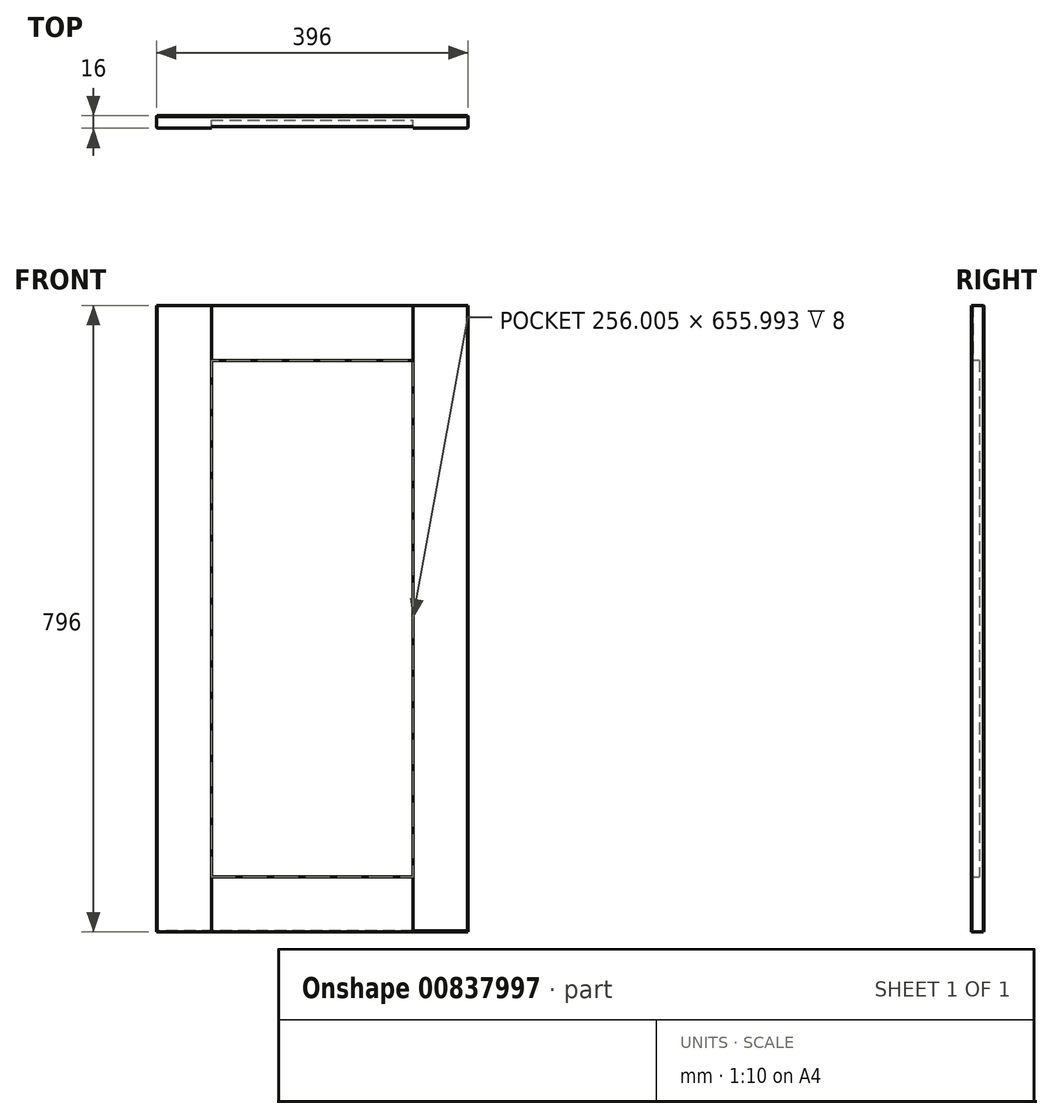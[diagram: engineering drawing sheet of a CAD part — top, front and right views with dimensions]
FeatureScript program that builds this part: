
annotation { "Feature Type Name" : "Feature", "Feature Type Description" : "" }
export const myFeature = defineFeature(function(context is Context, id is Id, definition is map)
    precondition{}
    {
        {
            var Q0;
            Q0=qCreatedBy(makeId("Front.planeOp"),FACE);
            var sketch = newSketch(context, id + "F0", { "sketchPlane" : qUnion([Q0])});
            skLineSegment(sketch, "E0.bottom", {"start": v(0, 0) * mm, "end": v(35.9, 0) * mm});
            skLineSegment(sketch, "E0.top", {"start": v(0, 30.12) * mm, "end": v(35.9, 30.12) * mm});
            skLineSegment(sketch, "E0.left", {"start": v(0, 0) * mm, "end": v(0, 30.12) * mm});
            skLineSegment(sketch, "E0.right", {"start": v(35.9, 0) * mm, "end": v(35.9, 30.12) * mm});
            skSolve(sketch);
        }
        {
            var Q0;
            Q0=makeQuery(id+"F0.imprint","IMPRINT",FACE,{"disambiguationData":[TD([[makeQuery(id+"F0.imprint","IMPRINT",EDGE,{"derivedFrom":sQuery(id+"F0.wireOp",EDGE,"E0.bottom")}),1.0]])]});
            extrude(context, id + "F1", {"entities" : qUnion([Q0]), "depth" : 16 * mm, "offsetDistance" : 25.4 * mm});
        }
        {
            var Q0;
            Q0=makeQuery(id+"F1.opExtrude","SWEPT_FACE",FACE,{"disambiguationData":[OSD([sQuery(id+"F0.wireOp",EDGE,"E0.left")])]});
            extrude(context, id + "F2", {"entities" : qUnion([Q0]), "operationType" : NewBodyOperationType.ADD, "oppositeDirection" : true, "depth" : 196 * mm, "offsetDistance" : 25 * mm});
        }
        {
            var Q0;
            {var subQ0=sQuery(id+"F0.wireOp",EDGE,"E0.bottom");Q0=makeQuery(id+"F2.boolean.opBoolean","MERGE",FACE,{"derivedFrom":[makeQuery(id+"F1.opExtrude","SWEPT_FACE",FACE,{"disambiguationData":[OSD([subQ0])]}),makeQuery(id+"F2.opExtrude","SWEPT_FACE",FACE,{"disambiguationData":[OSD([subQ0,sQuery(id+"F0.wireOp",EDGE,"E0.left")])]})]});}
            extrude(context, id + "F3", {"entities" : qUnion([Q0]), "operationType" : NewBodyOperationType.ADD, "oppositeDirection" : true, "depth" : 796 * mm, "offsetDistance" : 25 * mm});
        }
        {
            var Q0;
            {var subQ0=sQuery(id+"F0.wireOp",EDGE,"E0.left");var subQ1=sQuery(id+"F0.wireOp",EDGE,"E0.bottom");Q0=makeQuery(id+"F3.boolean.opBoolean","MERGE",FACE,{"derivedFrom":[makeQuery(id+"F2.boolean.opBoolean","MERGE",FACE,{"derivedFrom":[makeQuery(id+"F1.opExtrude","CAP_FACE",FACE,{"disambiguationData":[OSD([subQ1,sQuery(id+"F0.wireOp",EDGE,"E0.top"),subQ0,sQuery(id+"F0.wireOp",EDGE,"E0.right")])],"isStart":false}),makeQuery(id+"F2.opExtrude","SWEPT_FACE",FACE,{"disambiguationData":[OSD([subQ0]),TDD([makeQuery(id+"F1.opExtrude","CAP_EDGE",EDGE,{"disambiguationData":[OSD([subQ0])],"isStart":false})])]})]}),makeQuery(id+"F3.opExtrude","SWEPT_FACE",FACE,{"disambiguationData":[OSD([subQ1,subQ0]),TDD([makeQuery(id+"F2.boolean.opBoolean","MERGE",EDGE,{"derivedFrom":[makeQuery(id+"F1.opExtrude","CAP_EDGE",EDGE,{"disambiguationData":[OSD([subQ1])],"isStart":false}),makeQuery(id+"F2.opExtrude","SWEPT_EDGE",EDGE,{"disambiguationData":[OSD([subQ1,subQ0]),TDD([makeQuery(id+"F1.opExtrude","CAP_VERTEX",VERTEX,{"disambiguationData":[OSD([subQ1,subQ0])],"isStart":false})])]})]})])]})]});}
            var sketch = newSketch(context, id + "F4", { "sketchPlane" : qUnion([Q0])});
            skLineSegment(sketch, "E1.bottom", {"start": v(0, 796) * mm, "end": v(42.19, 796) * mm});
            skLineSegment(sketch, "E1.top", {"start": v(0, 751.57) * mm, "end": v(42.19, 751.57) * mm});
            skLineSegment(sketch, "E1.left", {"start": v(0, 796) * mm, "end": v(0, 751.57) * mm});
            skLineSegment(sketch, "E1.right", {"start": v(42.19, 796) * mm, "end": v(42.19, 751.57) * mm});
            skLineSegment(sketch, "E2.bottom", {"start": v(196, 796) * mm, "end": v(153.6, 796) * mm});
            skLineSegment(sketch, "E2.top", {"start": v(196, 746.75) * mm, "end": v(153.6, 746.75) * mm});
            skLineSegment(sketch, "E2.left", {"start": v(196, 796) * mm, "end": v(196, 746.75) * mm});
            skLineSegment(sketch, "E2.right", {"start": v(153.6, 796) * mm, "end": v(153.6, 746.75) * mm});
            skSolve(sketch);
        }
        {
            var Q0;
            Q0=makeQuery(id+"F4.imprint","IMPRINT",FACE,{"disambiguationData":[TD([[makeQuery(id+"F4.imprint","IMPRINT",EDGE,{"derivedFrom":sQuery(id+"F4.wireOp",EDGE,"E1.bottom")}),-1.0]])]});
            var Q1;
            Q1=makeQuery(id+"F4.imprint","IMPRINT",FACE,{"disambiguationData":[TD([[makeQuery(id+"F4.imprint","IMPRINT",EDGE,{"derivedFrom":sQuery(id+"F4.wireOp",EDGE,"E2.bottom")}),-1.0]])]});
            extrude(context, id + "F5", {"entities" : qUnion([Q0, Q1]), "operationType" : NewBodyOperationType.ADD, "depth" : 25 * mm, "offsetDistance" : 25 * mm});
        }
        {
            var Q0;
            {var subQ0=sQuery(id+"F0.wireOp",EDGE,"E0.left");var subQ1=sQuery(id+"F0.wireOp",EDGE,"E0.bottom");Q0=makeQuery(id+"F3.boolean.opBoolean","MERGE",FACE,{"derivedFrom":[makeQuery(id+"F2.boolean.opBoolean","MERGE",FACE,{"derivedFrom":[makeQuery(id+"F1.opExtrude","CAP_FACE",FACE,{"disambiguationData":[OSD([subQ1,sQuery(id+"F0.wireOp",EDGE,"E0.top"),subQ0,sQuery(id+"F0.wireOp",EDGE,"E0.right")])],"isStart":false}),makeQuery(id+"F2.opExtrude","SWEPT_FACE",FACE,{"disambiguationData":[OSD([subQ0]),TDD([makeQuery(id+"F1.opExtrude","CAP_EDGE",EDGE,{"disambiguationData":[OSD([subQ0])],"isStart":false})])]})]}),makeQuery(id+"F3.opExtrude","SWEPT_FACE",FACE,{"disambiguationData":[OSD([subQ1,subQ0]),TDD([makeQuery(id+"F2.boolean.opBoolean","MERGE",EDGE,{"derivedFrom":[makeQuery(id+"F1.opExtrude","CAP_EDGE",EDGE,{"disambiguationData":[OSD([subQ1])],"isStart":false}),makeQuery(id+"F2.opExtrude","SWEPT_EDGE",EDGE,{"disambiguationData":[OSD([subQ1,subQ0]),TDD([makeQuery(id+"F1.opExtrude","CAP_VERTEX",VERTEX,{"disambiguationData":[OSD([subQ1,subQ0])],"isStart":false})])]})]})])]})]});}
            var sketch = newSketch(context, id + "F6", { "sketchPlane" : qUnion([Q0])});
            skLineSegment(sketch, "E3.bottom", {"start": v(196, 0) * mm, "end": v(163.38, 0) * mm});
            skLineSegment(sketch, "E3.top", {"start": v(196, 46.55) * mm, "end": v(163.38, 46.55) * mm});
            skLineSegment(sketch, "E3.left", {"start": v(196, 0) * mm, "end": v(196, 46.55) * mm});
            skLineSegment(sketch, "E3.right", {"start": v(163.38, 0) * mm, "end": v(163.38, 46.55) * mm});
            skLineSegment(sketch, "E4.bottom", {"start": v(0, 0) * mm, "end": v(50.28, 0) * mm});
            skLineSegment(sketch, "E4.top", {"start": v(0, 44.4) * mm, "end": v(50.28, 44.4) * mm});
            skLineSegment(sketch, "E4.left", {"start": v(0, 0) * mm, "end": v(0, 44.4) * mm});
            skLineSegment(sketch, "E4.right", {"start": v(50.28, 0) * mm, "end": v(50.28, 44.4) * mm});
            skSolve(sketch);
        }
        {
            var Q0;
            Q0=makeQuery(id+"F6.imprint","IMPRINT",FACE,{"disambiguationData":[TD([[makeQuery(id+"F6.imprint","IMPRINT",EDGE,{"derivedFrom":sQuery(id+"F6.wireOp",EDGE,"E3.bottom")}),1.0]])]});
            var Q1;
            Q1=makeQuery(id+"F6.imprint","IMPRINT",FACE,{"disambiguationData":[TD([[makeQuery(id+"F6.imprint","IMPRINT",EDGE,{"derivedFrom":sQuery(id+"F6.wireOp",EDGE,"E4.bottom")}),1.0]])]});
            extrude(context, id + "F7", {"entities" : qUnion([Q0, Q1]), "operationType" : NewBodyOperationType.ADD, "depth" : 25 * mm, "offsetDistance" : 25 * mm});
        }
        {
            var Q0;
            Q0=makeQuery(id+"F7.opExtrude","SWEPT_FACE",FACE,{"disambiguationData":[OSD([sQuery(id+"F6.wireOp",EDGE,"E4.right")])]});
            extrude(context, id + "F8", {"entities" : qUnion([Q0]), "operationType" : NewBodyOperationType.ADD, "depth" : 19.72 * mm, "offsetDistance" : 25 * mm});
        }
        {
            var Q0;
            {var subQ0=sQuery(id+"F6.wireOp",EDGE,"E4.top");Q0=makeQuery(id+"F8.boolean.opBoolean","MERGE",FACE,{"derivedFrom":[makeQuery(id+"F7.opExtrude","SWEPT_FACE",FACE,{"disambiguationData":[OSD([subQ0])]}),makeQuery(id+"F8.opExtrude","SWEPT_FACE",FACE,{"disambiguationData":[OSD([subQ0,sQuery(id+"F6.wireOp",EDGE,"E4.right")])]})]});}
            extrude(context, id + "F9", {"entities" : qUnion([Q0]), "operationType" : NewBodyOperationType.ADD, "depth" : 25.6 * mm, "offsetDistance" : 25 * mm});
        }
        {
            var Q0;
            Q0=makeQuery(id+"F7.opExtrude","SWEPT_FACE",FACE,{"disambiguationData":[OSD([sQuery(id+"F6.wireOp",EDGE,"E3.right")])]});
            extrude(context, id + "F10", {"entities" : qUnion([Q0]), "operationType" : NewBodyOperationType.ADD, "depth" : 37.38 * mm, "offsetDistance" : 25 * mm});
        }
        {
            var Q0;
            {var subQ0=sQuery(id+"F6.wireOp",EDGE,"E3.top");Q0=makeQuery(id+"F10.boolean.opBoolean","MERGE",FACE,{"derivedFrom":[makeQuery(id+"F7.opExtrude","SWEPT_FACE",FACE,{"disambiguationData":[OSD([subQ0])]}),makeQuery(id+"F10.opExtrude","SWEPT_FACE",FACE,{"disambiguationData":[OSD([subQ0,sQuery(id+"F6.wireOp",EDGE,"E3.right")])]})]});}
            extrude(context, id + "F11", {"entities" : qUnion([Q0]), "operationType" : NewBodyOperationType.ADD, "depth" : 23.45 * mm, "offsetDistance" : 25 * mm});
        }
        {
            var Q0;
            Q0=makeQuery(id+"F5.opExtrude","SWEPT_FACE",FACE,{"disambiguationData":[OSD([sQuery(id+"F4.wireOp",EDGE,"E1.right")])]});
            extrude(context, id + "F12", {"entities" : qUnion([Q0]), "operationType" : NewBodyOperationType.ADD, "depth" : 27.8 * mm, "offsetDistance" : 25 * mm});
        }
        {
            var Q0;
            {var subQ0=sQuery(id+"F4.wireOp",EDGE,"E1.top");Q0=makeQuery(id+"F12.boolean.opBoolean","MERGE",FACE,{"derivedFrom":[makeQuery(id+"F5.opExtrude","SWEPT_FACE",FACE,{"disambiguationData":[OSD([subQ0])]}),makeQuery(id+"F12.opExtrude","SWEPT_FACE",FACE,{"disambiguationData":[OSD([subQ0,sQuery(id+"F4.wireOp",EDGE,"E1.right")])]})]});}
            extrude(context, id + "F13", {"entities" : qUnion([Q0]), "operationType" : NewBodyOperationType.ADD, "depth" : 25.57 * mm, "offsetDistance" : 25 * mm});
        }
        {
            var Q0;
            Q0=makeQuery(id+"F5.opExtrude","SWEPT_FACE",FACE,{"disambiguationData":[OSD([sQuery(id+"F4.wireOp",EDGE,"E2.top")])]});
            extrude(context, id + "F14", {"entities" : qUnion([Q0]), "operationType" : NewBodyOperationType.ADD, "depth" : 20.75 * mm, "offsetDistance" : 25 * mm});
        }
        {
            var Q0;
            {var subQ0=sQuery(id+"F4.wireOp",EDGE,"E2.right");Q0=makeQuery(id+"F14.boolean.opBoolean","MERGE",FACE,{"derivedFrom":[makeQuery(id+"F5.opExtrude","SWEPT_FACE",FACE,{"disambiguationData":[OSD([subQ0])]}),makeQuery(id+"F14.opExtrude","SWEPT_FACE",FACE,{"disambiguationData":[OSD([sQuery(id+"F4.wireOp",EDGE,"E2.top"),subQ0])]})]});}
            extrude(context, id + "F15", {"entities" : qUnion([Q0]), "operationType" : NewBodyOperationType.ADD, "depth" : 27.6 * mm, "offsetDistance" : 25 * mm});
        }
        {
            var Q0;
            {var subQ0=sQuery(id+"F0.wireOp",EDGE,"E0.left");var subQ1=sQuery(id+"F0.wireOp",EDGE,"E0.bottom");Q0=makeQuery(id+"F3.boolean.opBoolean","MERGE",FACE,{"derivedFrom":[makeQuery(id+"F2.boolean.opBoolean","MERGE",FACE,{"derivedFrom":[makeQuery(id+"F1.opExtrude","CAP_FACE",FACE,{"disambiguationData":[OSD([subQ1,sQuery(id+"F0.wireOp",EDGE,"E0.top"),subQ0,sQuery(id+"F0.wireOp",EDGE,"E0.right")])],"isStart":false}),makeQuery(id+"F2.opExtrude","SWEPT_FACE",FACE,{"disambiguationData":[OSD([subQ0]),TDD([makeQuery(id+"F1.opExtrude","CAP_EDGE",EDGE,{"disambiguationData":[OSD([subQ0])],"isStart":false})])]})]}),makeQuery(id+"F3.opExtrude","SWEPT_FACE",FACE,{"disambiguationData":[OSD([subQ1,subQ0]),TDD([makeQuery(id+"F2.boolean.opBoolean","MERGE",EDGE,{"derivedFrom":[makeQuery(id+"F1.opExtrude","CAP_EDGE",EDGE,{"disambiguationData":[OSD([subQ1])],"isStart":false}),makeQuery(id+"F2.opExtrude","SWEPT_EDGE",EDGE,{"disambiguationData":[OSD([subQ1,subQ0]),TDD([makeQuery(id+"F1.opExtrude","CAP_VERTEX",VERTEX,{"disambiguationData":[OSD([subQ1,subQ0])],"isStart":false})])]})]})])]})]});}
            var sketch = newSketch(context, id + "F16", { "sketchPlane" : qUnion([Q0])});
            skLineSegment(sketch, "E5.bottom", {"start": v(70, 726) * mm, "end": v(126, 726) * mm});
            skLineSegment(sketch, "E5.top", {"start": v(70, 70) * mm, "end": v(126, 70) * mm});
            skLineSegment(sketch, "E5.left", {"start": v(70, 726) * mm, "end": v(70, 70) * mm});
            skLineSegment(sketch, "E5.right", {"start": v(126, 726) * mm, "end": v(126, 70) * mm});
            skSolve(sketch);
        }
        {
            var Q0;
            Q0=makeQuery(id+"F16.imprint","IMPRINT",FACE,{"disambiguationData":[TD([[makeQuery(id+"F16.imprint","IMPRINT",EDGE,{"derivedFrom":sQuery(id+"F16.wireOp",EDGE,"E5.top")}),1.0]])]});
            extrude(context, id + "F17", {"entities" : qUnion([Q0]), "operationType" : NewBodyOperationType.REMOVE, "oppositeDirection" : true, "depth" : 10 * mm, "offsetDistance" : 25 * mm});
        }
        {
            var Q0;
            {var subQ2=sQuery(id+"F0.wireOp",EDGE,"E0.left");var subQ3=sQuery(id+"F0.wireOp",EDGE,"E0.bottom");var subQ4=makeQuery(id+"F1.opExtrude","CAP_FACE",FACE,{"disambiguationData":[OSD([subQ3,sQuery(id+"F0.wireOp",EDGE,"E0.top"),subQ2,sQuery(id+"F0.wireOp",EDGE,"E0.right")])],"isStart":false});var subQ7=makeQuery(id+"F3.opExtrude","SWEPT_FACE",FACE,{"disambiguationData":[OSD([subQ3,subQ2]),TDD([makeQuery(id+"F2.boolean.opBoolean","MERGE",EDGE,{"derivedFrom":[makeQuery(id+"F1.opExtrude","CAP_EDGE",EDGE,{"disambiguationData":[OSD([subQ3])],"isStart":false}),makeQuery(id+"F2.opExtrude","SWEPT_EDGE",EDGE,{"disambiguationData":[OSD([subQ3,subQ2]),TDD([makeQuery(id+"F1.opExtrude","CAP_VERTEX",VERTEX,{"disambiguationData":[OSD([subQ3,subQ2])],"isStart":false})])]})]})])]});var subQ8=makeQuery(id+"F2.opExtrude","SWEPT_FACE",FACE,{"disambiguationData":[OSD([subQ2]),TDD([makeQuery(id+"F1.opExtrude","CAP_EDGE",EDGE,{"disambiguationData":[OSD([subQ2])],"isStart":false})])]});Q0=makeQuery(id+"F17.boolean.opBoolean","SPLIT",FACE,{"disambiguationData":[TD([makeQuery(id+"F1.opExtrude","SWEPT_FACE",FACE,{"disambiguationData":[OSD([subQ3])]})])],"derivedFrom":makeQuery(id+"F3.boolean.opBoolean","MERGE",FACE,{"derivedFrom":[makeQuery(id+"F2.boolean.opBoolean","MERGE",FACE,{"derivedFrom":[subQ4,subQ8]}),subQ7]})});}
            var Q1;
            {var subQ2=sQuery(id+"F4.wireOp",EDGE,"E1.bottom");var subQ3=sQuery(id+"F0.wireOp",EDGE,"E0.left");var subQ4=sQuery(id+"F0.wireOp",EDGE,"E0.bottom");var subQ6=makeQuery(id+"F1.opExtrude","CAP_FACE",FACE,{"disambiguationData":[OSD([subQ4,sQuery(id+"F0.wireOp",EDGE,"E0.top"),subQ3,sQuery(id+"F0.wireOp",EDGE,"E0.right")])],"isStart":false});var subQ7=makeQuery(id+"F2.opExtrude","SWEPT_FACE",FACE,{"disambiguationData":[OSD([subQ3]),TDD([makeQuery(id+"F1.opExtrude","CAP_EDGE",EDGE,{"disambiguationData":[OSD([subQ3])],"isStart":false})])]});var subQ8=makeQuery(id+"F3.opExtrude","SWEPT_FACE",FACE,{"disambiguationData":[OSD([subQ4,subQ3]),TDD([makeQuery(id+"F2.boolean.opBoolean","MERGE",EDGE,{"derivedFrom":[makeQuery(id+"F1.opExtrude","CAP_EDGE",EDGE,{"disambiguationData":[OSD([subQ4])],"isStart":false}),makeQuery(id+"F2.opExtrude","SWEPT_EDGE",EDGE,{"disambiguationData":[OSD([subQ4,subQ3]),TDD([makeQuery(id+"F1.opExtrude","CAP_VERTEX",VERTEX,{"disambiguationData":[OSD([subQ4,subQ3])],"isStart":false})])]})]})])]});Q1=makeQuery(id+"F17.boolean.opBoolean","SPLIT",FACE,{"disambiguationData":[TD([makeQuery(id+"F5.opExtrude","SWEPT_FACE",FACE,{"disambiguationData":[OSD([subQ2])]})])],"derivedFrom":makeQuery(id+"F3.boolean.opBoolean","MERGE",FACE,{"derivedFrom":[makeQuery(id+"F2.boolean.opBoolean","MERGE",FACE,{"derivedFrom":[subQ6,subQ7]}),subQ8]})});}
            extrude(context, id + "F18", {"entities" : qUnion([Q0, Q1]), "operationType" : NewBodyOperationType.REMOVE, "oppositeDirection" : true, "depth" : 2 * mm, "offsetDistance" : 25 * mm});
        }
        {
            var Q0;
            {var subQ0=sQuery(id+"F4.wireOp",EDGE,"E1.right");var subQ1=sQuery(id+"F4.wireOp",EDGE,"E1.top");Q0=makeQuery(id+"F13.boolean.opBoolean","MERGE",FACE,{"derivedFrom":[makeQuery(id+"F12.boolean.opBoolean","MERGE",FACE,{"derivedFrom":[makeQuery(id+"F5.opExtrude","CAP_FACE",FACE,{"disambiguationData":[OSD([sQuery(id+"F4.wireOp",EDGE,"E1.bottom"),subQ1,sQuery(id+"F4.wireOp",EDGE,"E1.left"),subQ0])],"isStart":false}),makeQuery(id+"F12.opExtrude","SWEPT_FACE",FACE,{"disambiguationData":[OSD([subQ0]),TDD([makeQuery(id+"F5.opExtrude","CAP_EDGE",EDGE,{"disambiguationData":[OSD([subQ0])],"isStart":false})])]})]}),makeQuery(id+"F13.opExtrude","SWEPT_FACE",FACE,{"disambiguationData":[OSD([subQ1,subQ0]),TDD([makeQuery(id+"F12.boolean.opBoolean","MERGE",EDGE,{"derivedFrom":[makeQuery(id+"F5.opExtrude","CAP_EDGE",EDGE,{"disambiguationData":[OSD([subQ1])],"isStart":false}),makeQuery(id+"F12.opExtrude","SWEPT_EDGE",EDGE,{"disambiguationData":[OSD([subQ1,subQ0]),TDD([makeQuery(id+"F5.opExtrude","CAP_VERTEX",VERTEX,{"disambiguationData":[OSD([subQ1,subQ0])],"isStart":false})])]})]})])]})]});}
            var Q1;
            {var subQ0=sQuery(id+"F4.wireOp",EDGE,"E2.right");var subQ1=sQuery(id+"F4.wireOp",EDGE,"E2.top");Q1=makeQuery(id+"F15.boolean.opBoolean","MERGE",FACE,{"derivedFrom":[makeQuery(id+"F14.boolean.opBoolean","MERGE",FACE,{"derivedFrom":[makeQuery(id+"F5.opExtrude","CAP_FACE",FACE,{"disambiguationData":[OSD([sQuery(id+"F4.wireOp",EDGE,"E2.bottom"),subQ1,sQuery(id+"F4.wireOp",EDGE,"E2.left"),subQ0])],"isStart":false}),makeQuery(id+"F14.opExtrude","SWEPT_FACE",FACE,{"disambiguationData":[OSD([subQ1]),TDD([makeQuery(id+"F5.opExtrude","CAP_EDGE",EDGE,{"disambiguationData":[OSD([subQ1])],"isStart":false})])]})]}),makeQuery(id+"F15.opExtrude","SWEPT_FACE",FACE,{"disambiguationData":[OSD([subQ1,subQ0]),TDD([makeQuery(id+"F14.boolean.opBoolean","MERGE",EDGE,{"derivedFrom":[makeQuery(id+"F5.opExtrude","CAP_EDGE",EDGE,{"disambiguationData":[OSD([subQ0])],"isStart":false}),makeQuery(id+"F14.opExtrude","SWEPT_EDGE",EDGE,{"disambiguationData":[OSD([subQ1,subQ0]),TDD([makeQuery(id+"F5.opExtrude","CAP_VERTEX",VERTEX,{"disambiguationData":[OSD([subQ1,subQ0])],"isStart":false})])]})]})])]})]});}
            var Q2;
            {var subQ0=sQuery(id+"F6.wireOp",EDGE,"E4.right");var subQ1=sQuery(id+"F6.wireOp",EDGE,"E4.top");Q2=makeQuery(id+"F9.boolean.opBoolean","MERGE",FACE,{"derivedFrom":[makeQuery(id+"F8.boolean.opBoolean","MERGE",FACE,{"derivedFrom":[makeQuery(id+"F7.opExtrude","CAP_FACE",FACE,{"disambiguationData":[OSD([sQuery(id+"F6.wireOp",EDGE,"E4.bottom"),subQ1,sQuery(id+"F6.wireOp",EDGE,"E4.left"),subQ0])],"isStart":false}),makeQuery(id+"F8.opExtrude","SWEPT_FACE",FACE,{"disambiguationData":[OSD([subQ0]),TDD([makeQuery(id+"F7.opExtrude","CAP_EDGE",EDGE,{"disambiguationData":[OSD([subQ0])],"isStart":false})])]})]}),makeQuery(id+"F9.opExtrude","SWEPT_FACE",FACE,{"disambiguationData":[OSD([subQ1,subQ0]),TDD([makeQuery(id+"F8.boolean.opBoolean","MERGE",EDGE,{"derivedFrom":[makeQuery(id+"F7.opExtrude","CAP_EDGE",EDGE,{"disambiguationData":[OSD([subQ1])],"isStart":false}),makeQuery(id+"F8.opExtrude","SWEPT_EDGE",EDGE,{"disambiguationData":[OSD([subQ1,subQ0]),TDD([makeQuery(id+"F7.opExtrude","CAP_VERTEX",VERTEX,{"disambiguationData":[OSD([subQ1,subQ0])],"isStart":false})])]})]})])]})]});}
            var Q3;
            {var subQ0=sQuery(id+"F6.wireOp",EDGE,"E3.right");var subQ1=sQuery(id+"F6.wireOp",EDGE,"E3.top");Q3=makeQuery(id+"F11.boolean.opBoolean","MERGE",FACE,{"derivedFrom":[makeQuery(id+"F10.boolean.opBoolean","MERGE",FACE,{"derivedFrom":[makeQuery(id+"F7.opExtrude","CAP_FACE",FACE,{"disambiguationData":[OSD([sQuery(id+"F6.wireOp",EDGE,"E3.bottom"),subQ1,sQuery(id+"F6.wireOp",EDGE,"E3.left"),subQ0])],"isStart":false}),makeQuery(id+"F10.opExtrude","SWEPT_FACE",FACE,{"disambiguationData":[OSD([subQ0]),TDD([makeQuery(id+"F7.opExtrude","CAP_EDGE",EDGE,{"disambiguationData":[OSD([subQ0])],"isStart":false})])]})]}),makeQuery(id+"F11.opExtrude","SWEPT_FACE",FACE,{"disambiguationData":[OSD([subQ1,subQ0]),TDD([makeQuery(id+"F10.boolean.opBoolean","MERGE",EDGE,{"derivedFrom":[makeQuery(id+"F7.opExtrude","CAP_EDGE",EDGE,{"disambiguationData":[OSD([subQ1])],"isStart":false}),makeQuery(id+"F10.opExtrude","SWEPT_EDGE",EDGE,{"disambiguationData":[OSD([subQ1,subQ0]),TDD([makeQuery(id+"F7.opExtrude","CAP_VERTEX",VERTEX,{"disambiguationData":[OSD([subQ1,subQ0])],"isStart":false})])]})]})])]})]});}
            extrude(context, id + "F19", {"entities" : qUnion([Q0, Q1, Q2, Q3]), "operationType" : NewBodyOperationType.REMOVE, "oppositeDirection" : true, "depth" : 25 * mm, "offsetDistance" : 25 * mm});
        }
        {
            var Q0;
            {var subQ0=sQuery(id+"F4.wireOp",EDGE,"E2.left");var subQ1=sQuery(id+"F0.wireOp",EDGE,"E0.left");var subQ2=sQuery(id+"F0.wireOp",EDGE,"E0.bottom");var subQ3=sQuery(id+"F6.wireOp",EDGE,"E3.left");Q0=makeQuery(id+"F14.boolean.opBoolean","MERGE",FACE,{"derivedFrom":[makeQuery(id+"F11.boolean.opBoolean","MERGE",FACE,{"derivedFrom":[makeQuery(id+"F7.boolean.opBoolean","MERGE",FACE,{"derivedFrom":[makeQuery(id+"F5.boolean.opBoolean","MERGE",FACE,{"derivedFrom":[makeQuery(id+"F3.boolean.opBoolean","MERGE",FACE,{"derivedFrom":[makeQuery(id+"F2.opExtrude","CAP_FACE",FACE,{"disambiguationData":[OSD([subQ1])],"isStart":false}),makeQuery(id+"F3.opExtrude","SWEPT_FACE",FACE,{"disambiguationData":[OSD([subQ2,subQ1]),TDD([makeQuery(id+"F2.opExtrude","CAP_EDGE",EDGE,{"disambiguationData":[OSD([subQ2,subQ1])],"isStart":false})])]})]}),makeQuery(id+"F5.opExtrude","SWEPT_FACE",FACE,{"disambiguationData":[OSD([subQ0])]})]}),makeQuery(id+"F7.opExtrude","SWEPT_FACE",FACE,{"disambiguationData":[OSD([subQ3])]})]}),makeQuery(id+"F11.opExtrude","SWEPT_FACE",FACE,{"disambiguationData":[OSD([subQ2,subQ1,sQuery(id+"F6.wireOp",EDGE,"E3.top"),subQ3])]})]}),makeQuery(id+"F14.opExtrude","SWEPT_FACE",FACE,{"disambiguationData":[OSD([subQ2,subQ1,sQuery(id+"F4.wireOp",EDGE,"E2.top"),subQ0])]})]});}
            extrude(context, id + "F20", {"entities" : qUnion([Q0]), "operationType" : NewBodyOperationType.ADD, "depth" : 200 * mm, "offsetDistance" : 25 * mm});
        }
        {
            var Q0;
            {var subQ0=sQuery(id+"F4.wireOp",EDGE,"E2.right");var subQ1=sQuery(id+"F4.wireOp",EDGE,"E2.top");Q0=makeQuery(id+"F18.boolean.opBoolean","MERGE",FACE,{"derivedFrom":[makeQuery(id+"F15.opExtrude","CAP_FACE",FACE,{"disambiguationData":[OSD([subQ1,subQ0])],"isStart":false}),makeQuery(id+"F18.opExtrude","SWEPT_FACE",FACE,{"disambiguationData":[OSD([subQ1,subQ0])]})]});}
            var Q1;
            {var subQ0=sQuery(id+"F6.wireOp",EDGE,"E3.right");var subQ1=sQuery(id+"F6.wireOp",EDGE,"E3.top");Q1=makeQuery(id+"F18.boolean.opBoolean","MERGE",FACE,{"derivedFrom":[makeQuery(id+"F11.boolean.opBoolean","MERGE",FACE,{"derivedFrom":[makeQuery(id+"F10.opExtrude","CAP_FACE",FACE,{"disambiguationData":[OSD([subQ0])],"isStart":false}),makeQuery(id+"F11.opExtrude","SWEPT_FACE",FACE,{"disambiguationData":[OSD([subQ1,subQ0]),TDD([makeQuery(id+"F10.opExtrude","CAP_EDGE",EDGE,{"disambiguationData":[OSD([subQ1,subQ0])],"isStart":false})])]})]}),makeQuery(id+"F17.boolean.opBoolean","COPY",FACE,{"derivedFrom":makeQuery(id+"F17.opExtrude","SWEPT_FACE",FACE,{"disambiguationData":[OSD([sQuery(id+"F16.wireOp",EDGE,"E5.right")])]})}),makeQuery(id+"F18.opExtrude","SWEPT_FACE",FACE,{"disambiguationData":[OSD([subQ1,subQ0])]})]});}
            extrude(context, id + "F21", {"entities" : qUnion([Q0, Q1]), "operationType" : NewBodyOperationType.REMOVE, "oppositeDirection" : true, "depth" : 200 * mm, "offsetDistance" : 25 * mm});
        }
        {
            var Q0;
            {var subQ0=sQuery(id+"F4.wireOp",EDGE,"E2.bottom");var subQ1=sQuery(id+"F0.wireOp",EDGE,"E0.left");var subQ2=sQuery(id+"F0.wireOp",EDGE,"E0.bottom");var subQ3=sQuery(id+"F4.wireOp",EDGE,"E1.bottom");Q0=makeQuery(id+"F20.boolean.opBoolean","MERGE",FACE,{"derivedFrom":[makeQuery(id+"F15.boolean.opBoolean","MERGE",FACE,{"derivedFrom":[makeQuery(id+"F12.boolean.opBoolean","MERGE",FACE,{"derivedFrom":[makeQuery(id+"F5.boolean.opBoolean","MERGE",FACE,{"derivedFrom":[makeQuery(id+"F3.opExtrude","CAP_FACE",FACE,{"disambiguationData":[OSD([subQ2,subQ1])],"isStart":false}),makeQuery(id+"F5.opExtrude","SWEPT_FACE",FACE,{"disambiguationData":[OSD([subQ3])]}),makeQuery(id+"F5.opExtrude","SWEPT_FACE",FACE,{"disambiguationData":[OSD([subQ0])]})]}),makeQuery(id+"F12.opExtrude","SWEPT_FACE",FACE,{"disambiguationData":[OSD([subQ2,subQ1,subQ3,sQuery(id+"F4.wireOp",EDGE,"E1.right")])]})]}),makeQuery(id+"F15.opExtrude","SWEPT_FACE",FACE,{"disambiguationData":[OSD([subQ2,subQ1,subQ0,sQuery(id+"F4.wireOp",EDGE,"E2.right")])]})]}),makeQuery(id+"F20.opExtrude","SWEPT_FACE",FACE,{"disambiguationData":[OSD([subQ2,subQ1,subQ0,sQuery(id+"F4.wireOp",EDGE,"E2.left")])]})]});}
            extrude(context, id + "F22", {"entities" : qUnion([Q0]), "operationType" : NewBodyOperationType.ADD, "depth" : 200 * mm, "offsetDistance" : 25 * mm});
        }
        {
            var Q0;
            Q0=makeQuery(id+"F17.boolean.opBoolean","COPY",FACE,{"derivedFrom":makeQuery(id+"F17.opExtrude","SWEPT_FACE",FACE,{"disambiguationData":[OSD([sQuery(id+"F16.wireOp",EDGE,"E5.bottom")])]})});
            var Q1;
            {var subQ0=sQuery(id+"F16.wireOp",EDGE,"E5.right");var subQ1=sQuery(id+"F16.wireOp",EDGE,"E5.bottom");var subQ2=sQuery(id+"F4.wireOp",EDGE,"E2.right");var subQ3=sQuery(id+"F4.wireOp",EDGE,"E2.top");var subQ4=makeQuery(id+"F17.boolean.opBoolean","COPY",EDGE,{"derivedFrom":makeQuery(id+"F17.opExtrude","SWEPT_EDGE",EDGE,{"disambiguationData":[OSD([subQ3,subQ2,subQ1,subQ0])]})});Q1=makeQuery(id+"F21.boolean.opBoolean","COPY",FACE,{"derivedFrom":makeQuery(id+"F21.opExtrude","SWEPT_FACE",FACE,{"disambiguationData":[OSD([subQ3,subQ2,subQ1,subQ0]),TDD([makeQuery(id+"F18.boolean.opBoolean","MERGE",EDGE,{"derivedFrom":[subQ4,makeQuery(id+"F18.opExtrude","SWEPT_EDGE",EDGE,{"disambiguationData":[OSD([subQ3,subQ2,subQ1,subQ0])]})]}),makeQuery(id+"F18.boolean.opBoolean","SPLIT",EDGE,{"derivedFrom":subQ4})])]})});}
            extrude(context, id + "F23", {"entities" : qUnion([Q0, Q1]), "operationType" : NewBodyOperationType.REMOVE, "oppositeDirection" : true, "depth" : 200 * mm, "offsetDistance" : 25 * mm});
        }
        {
            var Q0;
            Q0=makeQuery(id+"F23.boolean.opBoolean","COPY",FACE,{"derivedFrom":makeQuery(id+"F23.opExtrude","CAP_FACE",FACE,{"disambiguationData":[OSD([sQuery(id+"F16.wireOp",EDGE,"E5.bottom")])],"isStart":false})});
            var Q1;
            Q1=makeQuery(id+"F23.boolean.opBoolean","COPY",FACE,{"derivedFrom":makeQuery(id+"F23.opExtrude","CAP_FACE",FACE,{"disambiguationData":[OSD([sQuery(id+"F4.wireOp",EDGE,"E2.top"),sQuery(id+"F4.wireOp",EDGE,"E2.right"),sQuery(id+"F16.wireOp",EDGE,"E5.bottom"),sQuery(id+"F16.wireOp",EDGE,"E5.right")])],"isStart":false})});
            extrude(context, id + "F24", {"entities" : qUnion([Q0, Q1]), "operationType" : NewBodyOperationType.ADD, "depth" : 200 * mm, "offsetDistance" : 25 * mm});
        }
        {
            var Q0;
            Q0=makeQuery(id+"F22.opExtrude","CAP_FACE",FACE,{"disambiguationData":[OSD([sQuery(id+"F0.wireOp",EDGE,"E0.bottom"),sQuery(id+"F0.wireOp",EDGE,"E0.left"),sQuery(id+"F4.wireOp",EDGE,"E1.bottom"),sQuery(id+"F4.wireOp",EDGE,"E1.right"),sQuery(id+"F4.wireOp",EDGE,"E2.bottom"),sQuery(id+"F4.wireOp",EDGE,"E2.left"),sQuery(id+"F4.wireOp",EDGE,"E2.right")])],"isStart":false});
            extrude(context, id + "F25", {"entities" : qUnion([Q0]), "operationType" : NewBodyOperationType.REMOVE, "oppositeDirection" : true, "depth" : 200 * mm, "offsetDistance" : 25 * mm});
        }
        {
            var Q0;
            {var subQ0=sQuery(id+"F4.wireOp",EDGE,"E2.left");Q0=makeQuery(id+"F22.boolean.opBoolean","MERGE",EDGE,{"derivedFrom":[makeQuery(id+"F20.opExtrude","CAP_EDGE",EDGE,{"disambiguationData":[OSD([sQuery(id+"F0.wireOp",EDGE,"E0.bottom"),sQuery(id+"F0.wireOp",EDGE,"E0.left"),sQuery(id+"F4.wireOp",EDGE,"E2.top"),subQ0,sQuery(id+"F6.wireOp",EDGE,"E3.top"),sQuery(id+"F6.wireOp",EDGE,"E3.left")])],"isStart":false}),makeQuery(id+"F22.opExtrude","SWEPT_EDGE",EDGE,{"disambiguationData":[OSD([sQuery(id+"F4.wireOp",EDGE,"E2.bottom"),subQ0])]})]});}
            var Q1;
            {var subQ0=sQuery(id+"F6.wireOp",EDGE,"E3.bottom");Q1=makeQuery(id+"F20.boolean.opBoolean","MERGE",EDGE,{"derivedFrom":[makeQuery(id+"F19.boolean.opBoolean","COPY",EDGE,{"derivedFrom":makeQuery(id+"F19.opExtrude","CAP_EDGE",EDGE,{"disambiguationData":[OSD([sQuery(id+"F0.wireOp",EDGE,"E0.bottom"),sQuery(id+"F0.wireOp",EDGE,"E0.left"),subQ0,sQuery(id+"F6.wireOp",EDGE,"E3.right")])],"isStart":false})}),makeQuery(id+"F20.opExtrude","SWEPT_EDGE",EDGE,{"disambiguationData":[OSD([subQ0,sQuery(id+"F6.wireOp",EDGE,"E3.left")])]})]});}
            var Q2;
            Q2=makeQuery(id+"F19.boolean.opBoolean","COPY",EDGE,{"derivedFrom":makeQuery(id+"F19.opExtrude","CAP_EDGE",EDGE,{"disambiguationData":[OSD([sQuery(id+"F0.wireOp",EDGE,"E0.bottom"),sQuery(id+"F0.wireOp",EDGE,"E0.left"),sQuery(id+"F6.wireOp",EDGE,"E4.bottom"),sQuery(id+"F6.wireOp",EDGE,"E4.right")])],"isStart":false})});
            var Q3;
            {var subQ0=sQuery(id+"F4.wireOp",EDGE,"E1.left");var subQ1=sQuery(id+"F0.wireOp",EDGE,"E0.left");var subQ2=sQuery(id+"F0.wireOp",EDGE,"E0.bottom");Q3=makeQuery(id+"F22.boolean.opBoolean","MERGE",EDGE,{"derivedFrom":[makeQuery(id+"F19.boolean.opBoolean","MERGE",EDGE,{"derivedFrom":[makeQuery(id+"F3.boolean.opBoolean","MERGE",EDGE,{"derivedFrom":[makeQuery(id+"F1.opExtrude","CAP_EDGE",EDGE,{"disambiguationData":[OSD([subQ1])],"isStart":false}),makeQuery(id+"F3.opExtrude","SWEPT_EDGE",EDGE,{"disambiguationData":[OSD([subQ2,subQ1]),TDD([makeQuery(id+"F1.opExtrude","CAP_VERTEX",VERTEX,{"disambiguationData":[OSD([subQ2,subQ1])],"isStart":false})])]})]}),makeQuery(id+"F19.opExtrude","CAP_EDGE",EDGE,{"disambiguationData":[OSD([subQ2,subQ1,sQuery(id+"F6.wireOp",EDGE,"E4.top"),sQuery(id+"F6.wireOp",EDGE,"E4.left")])],"isStart":false}),makeQuery(id+"F19.opExtrude","CAP_EDGE",EDGE,{"disambiguationData":[OSD([subQ2,subQ1,sQuery(id+"F4.wireOp",EDGE,"E1.top"),subQ0])],"isStart":false})]}),makeQuery(id+"F22.opExtrude","SWEPT_EDGE",EDGE,{"disambiguationData":[OSD([sQuery(id+"F4.wireOp",EDGE,"E1.bottom"),subQ0])]})]});}
            var Q4;
            {var subQ0=sQuery(id+"F4.wireOp",EDGE,"E1.right");var subQ1=sQuery(id+"F4.wireOp",EDGE,"E1.bottom");var subQ2=sQuery(id+"F0.wireOp",EDGE,"E0.left");var subQ3=sQuery(id+"F0.wireOp",EDGE,"E0.bottom");Q4=makeQuery(id+"F25.boolean.opBoolean","COPY",EDGE,{"derivedFrom":makeQuery(id+"F25.opExtrude","CAP_EDGE",EDGE,{"disambiguationData":[OSD([subQ3,subQ2,subQ1,subQ0]),TDD([makeQuery(id+"F22.opExtrude","CAP_EDGE",EDGE,{"disambiguationData":[OSD([subQ3,subQ2,subQ1,subQ0]),TDD([makeQuery(id+"F19.boolean.opBoolean","COPY",EDGE,{"derivedFrom":makeQuery(id+"F19.opExtrude","CAP_EDGE",EDGE,{"disambiguationData":[OSD([subQ3,subQ2,subQ1,subQ0])],"isStart":false})})])],"isStart":false})])],"isStart":false})});}
            var Q5;
            Q5=makeQuery(id+"F25.boolean.opBoolean","COPY",EDGE,{"derivedFrom":makeQuery(id+"F25.opExtrude","CAP_EDGE",EDGE,{"disambiguationData":[OSD([sQuery(id+"F0.wireOp",EDGE,"E0.bottom"),sQuery(id+"F0.wireOp",EDGE,"E0.left"),sQuery(id+"F4.wireOp",EDGE,"E2.bottom"),sQuery(id+"F4.wireOp",EDGE,"E2.left"),sQuery(id+"F4.wireOp",EDGE,"E2.right")])],"isStart":false})});
            var Q6;
            {var subQ0=sQuery(id+"F0.wireOp",EDGE,"E0.left");var subQ1=sQuery(id+"F0.wireOp",EDGE,"E0.bottom");Q6=makeQuery(id+"F22.boolean.opBoolean","MERGE",FACE,{"derivedFrom":[makeQuery(id+"F20.boolean.opBoolean","MERGE",FACE,{"derivedFrom":[makeQuery(id+"F3.boolean.opBoolean","MERGE",FACE,{"derivedFrom":[makeQuery(id+"F2.boolean.opBoolean","MERGE",FACE,{"derivedFrom":[makeQuery(id+"F1.opExtrude","CAP_FACE",FACE,{"disambiguationData":[OSD([subQ1,sQuery(id+"F0.wireOp",EDGE,"E0.top"),subQ0,sQuery(id+"F0.wireOp",EDGE,"E0.right")])],"isStart":true}),makeQuery(id+"F2.opExtrude","SWEPT_FACE",FACE,{"disambiguationData":[OSD([subQ0]),TDD([makeQuery(id+"F1.opExtrude","CAP_EDGE",EDGE,{"disambiguationData":[OSD([subQ0])],"isStart":true})])]})]}),makeQuery(id+"F3.opExtrude","SWEPT_FACE",FACE,{"disambiguationData":[OSD([subQ1,subQ0]),TDD([makeQuery(id+"F2.boolean.opBoolean","MERGE",EDGE,{"derivedFrom":[makeQuery(id+"F1.opExtrude","CAP_EDGE",EDGE,{"disambiguationData":[OSD([subQ1])],"isStart":true}),makeQuery(id+"F2.opExtrude","SWEPT_EDGE",EDGE,{"disambiguationData":[OSD([subQ1,subQ0]),TDD([makeQuery(id+"F1.opExtrude","CAP_VERTEX",VERTEX,{"disambiguationData":[OSD([subQ1,subQ0])],"isStart":true})])]})]})])]})]}),makeQuery(id+"F20.opExtrude","SWEPT_FACE",FACE,{"disambiguationData":[OSD([subQ1,subQ0])]})]}),makeQuery(id+"F22.opExtrude","SWEPT_FACE",FACE,{"disambiguationData":[OSD([subQ1,subQ0])]})]});}
            chamfer(context, id + "F26", {"entities" : qUnion([Q0, Q1, Q2, Q3, Q4, Q5, Q6]), "width" : 1 * mm, "tangentPropagation" : true});
        }
    });
